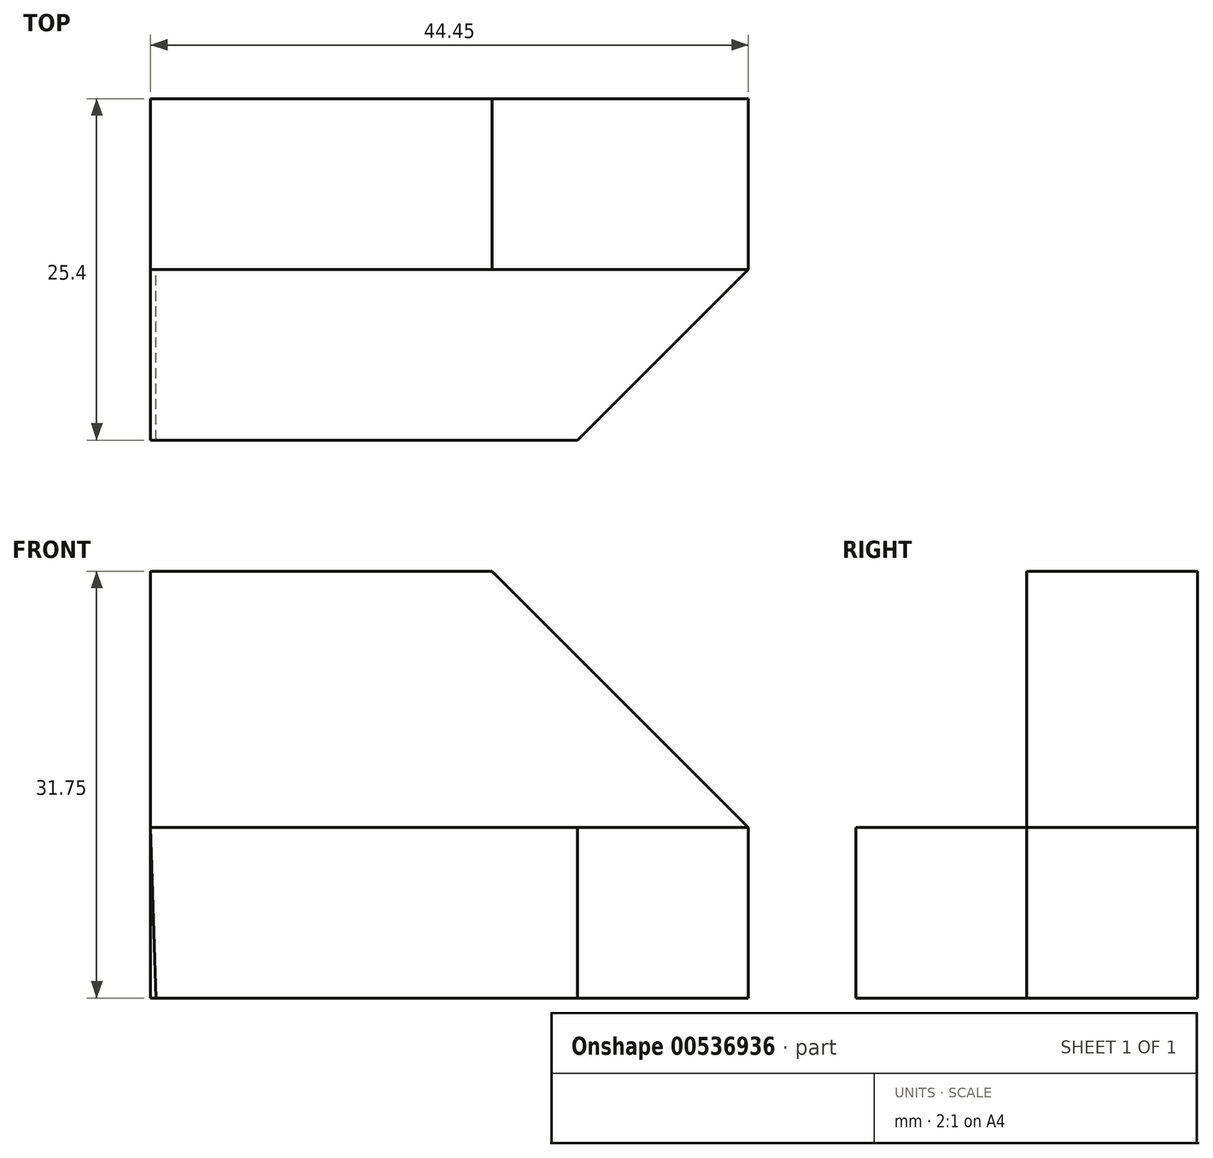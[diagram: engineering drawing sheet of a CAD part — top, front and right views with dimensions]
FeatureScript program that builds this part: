
annotation { "Feature Type Name" : "Feature", "Feature Type Description" : "" }
export const myFeature = defineFeature(function(context is Context, id is Id, definition is map)
    precondition{}
    {
        {
            var Q0;
            Q0=qCreatedBy(makeId("Front.planeOp"),FACE);
            var sketch = newSketch(context, id + "F0", { "sketchPlane" : qUnion([Q0])});
            skLineSegment(sketch, "E0.bottom", {"start": v(-44.45, 0) * mm, "end": v(0, 0) * mm});
            skLineSegment(sketch, "E0.top", {"start": v(-44.45, 31.75) * mm, "end": v(0, 31.75) * mm});
            skLineSegment(sketch, "E0.left", {"start": v(-44.45, 0) * mm, "end": v(-44.45, 31.75) * mm});
            skLineSegment(sketch, "E0.right", {"start": v(0, 0) * mm, "end": v(0, 31.75) * mm});
            skSolve(sketch);
        }
        {
            var Q0;
            Q0=makeQuery(id+"F0.imprint","IMPRINT",FACE,{"disambiguationData":[TD([[makeQuery(id+"F0.imprint","IMPRINT",EDGE,{"derivedFrom":sQuery(id+"F0.wireOp",EDGE,"E0.bottom")}),1.0]])]});
            var sketch = newSketch(context, id + "F1", { "sketchPlane" : qUnion([Q0])});
            skLineSegment(sketch, "E1", {"start": v(-44.45, 12.7) * mm, "end": v(0, 12.7) * mm});
            skLineSegment(sketch, "E2", {"start": v(0, 12.7) * mm, "end": v(0, 0) * mm});
            skLineSegment(sketch, "E3", {"start": v(0, 0) * mm, "end": v(-44.04, 0) * mm});
            skLineSegment(sketch, "E4", {"start": v(-44.04, 0) * mm, "end": v(-44.45, 12.7) * mm});
            skSolve(sketch);
        }
        {
            var Q0;
            Q0=makeQuery(id+"F1.imprint","IMPRINT",FACE,{"disambiguationData":[TD([[makeQuery(id+"F1.imprint","IMPRINT",EDGE,{"derivedFrom":sQuery(id+"F1.wireOp",EDGE,"E1")}),-1.0]])]});
            extrude(context, id + "F2", {"entities" : qUnion([Q0]), "depth" : 12.7 * mm, "offsetDistance" : 25.4 * mm});
        }
        {
            var Q0;
            Q0=makeQuery(id+"F0.imprint","IMPRINT",FACE,{"disambiguationData":[TD([[makeQuery(id+"F0.imprint","IMPRINT",EDGE,{"derivedFrom":sQuery(id+"F0.wireOp",EDGE,"E0.bottom")}),1.0]])]});
            extrude(context, id + "F3", {"entities" : qUnion([Q0]), "operationType" : NewBodyOperationType.ADD, "oppositeDirection" : true, "depth" : 12.7 * mm, "offsetDistance" : 25.4 * mm});
        }
        {
            var Q0;
            {var subQ0=sQuery(id+"F0.wireOp",EDGE,"E0.right");var subQ1=sQuery(id+"F0.wireOp",EDGE,"E0.left");var subQ2=sQuery(id+"F0.wireOp",EDGE,"E0.top");var subQ3=makeQuery(id+"F3.opExtrude","CAP_FACE",FACE,{"disambiguationData":[OSD([sQuery(id+"F0.wireOp",EDGE,"E0.bottom"),subQ2,subQ1,subQ0])],"isStart":true});Q0=makeQuery(id+"F3.boolean.opBoolean","SPLIT",FACE,{"disambiguationData":[TD([makeQuery(id+"F2.opExtrude","SWEPT_FACE",FACE,{"disambiguationData":[OSD([sQuery(id+"F1.wireOp",EDGE,"E2")])]})])],"derivedFrom":subQ3});}
            var sketch = newSketch(context, id + "F4", { "sketchPlane" : qUnion([Q0])});
            skLineSegment(sketch, "E5", {"start": v(-19.05, 31.75) * mm, "end": v(0, 12.7) * mm});
            skSolve(sketch);
        }
        {
            var Q0;
            {var subQ0=sQuery(id+"F4.wireOp",EDGE,"E5");Q0=makeQuery(id+"F4.imprint","IMPRINT",FACE,{"disambiguationData":[TD([[makeQuery(id+"F4.imprint","IMPRINT",EDGE,{"derivedFrom":subQ0}),1.0]])]});}
            extrude(context, id + "F5", {"entities" : qUnion([Q0]), "operationType" : NewBodyOperationType.REMOVE, "oppositeDirection" : true, "depth" : 25.4 * mm, "offsetDistance" : 25.4 * mm});
        }
        {
            var Q0;
            Q0=makeQuery(id+"F2.opExtrude","SWEPT_FACE",FACE,{"disambiguationData":[OSD([sQuery(id+"F1.wireOp",EDGE,"E1")])]});
            var sketch = newSketch(context, id + "F6", { "sketchPlane" : qUnion([Q0])});
            skLineSegment(sketch, "E6", {"start": v(-12.7, -12.7) * mm, "end": v(0, 0) * mm});
            skSolve(sketch);
        }
        {
            var Q0;
            {var subQ0=sQuery(id+"F6.wireOp",EDGE,"E6");Q0=makeQuery(id+"F6.imprint","IMPRINT",FACE,{"disambiguationData":[TD([[makeQuery(id+"F6.imprint","IMPRINT",EDGE,{"derivedFrom":subQ0}),-1.0]])]});}
            extrude(context, id + "F7", {"entities" : qUnion([Q0]), "operationType" : NewBodyOperationType.REMOVE, "oppositeDirection" : true, "depth" : 25.4 * mm, "offsetDistance" : 25.4 * mm});
        }
    });
